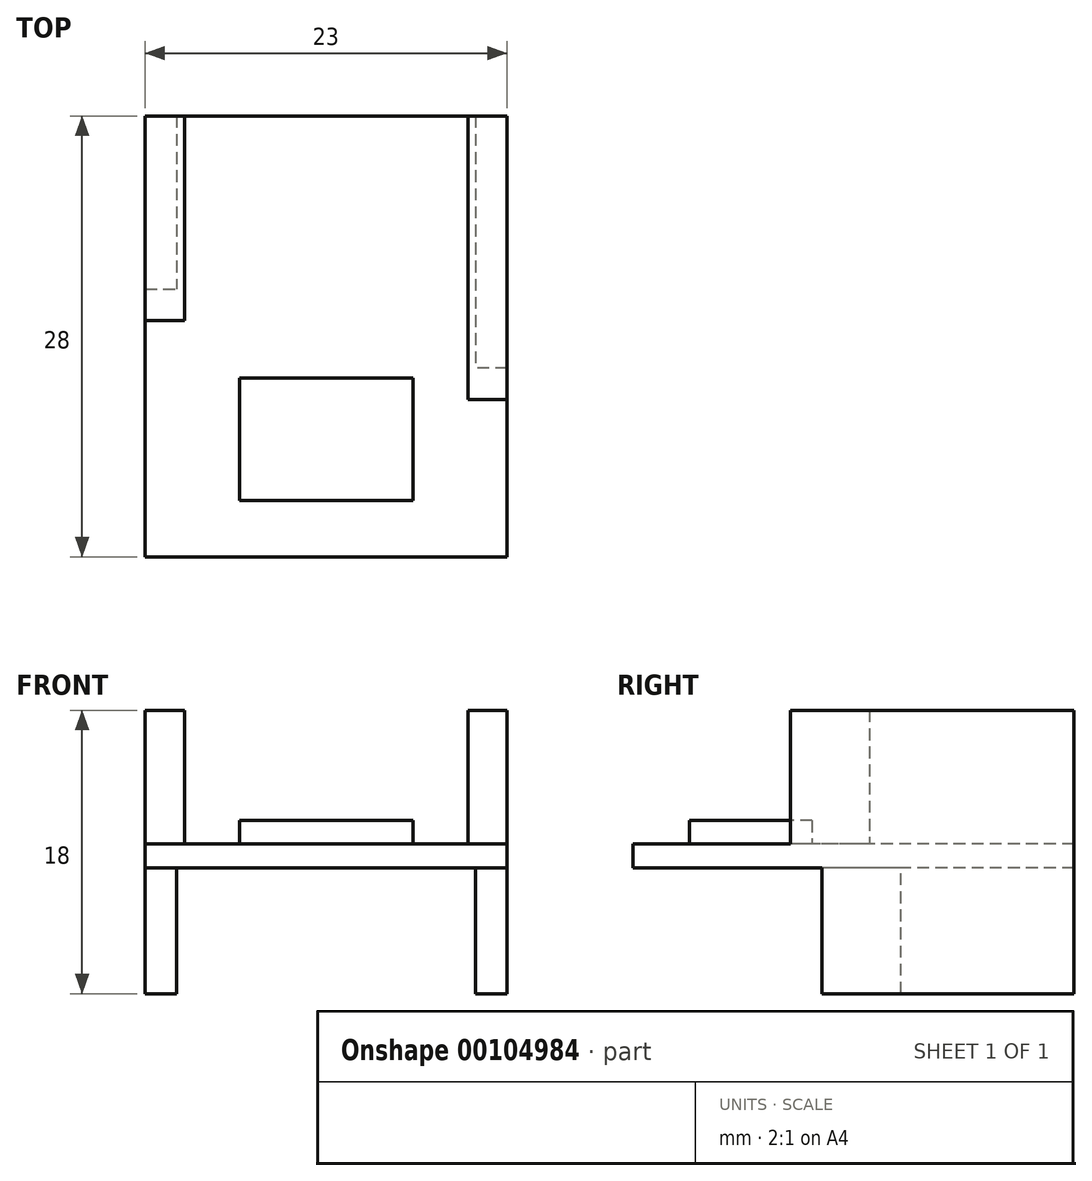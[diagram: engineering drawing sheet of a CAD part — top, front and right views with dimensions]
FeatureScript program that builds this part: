
annotation { "Feature Type Name" : "Feature", "Feature Type Description" : "" }
export const myFeature = defineFeature(function(context is Context, id is Id, definition is map)
    precondition{}
    {
        {
            var Q0;
            Q0=qCreatedBy(makeId("Top.planeOp"),FACE);
            var sketch = newSketch(context, id + "F0", { "sketchPlane" : qUnion([Q0])});
            skLineSegment(sketch, "E0.bottom", {"start": v(-11.5, 14) * mm, "end": v(11.5, 14) * mm});
            skLineSegment(sketch, "E0.top", {"start": v(-11.5, -14) * mm, "end": v(11.5, -14) * mm});
            skLineSegment(sketch, "E0.left", {"start": v(-11.5, 14) * mm, "end": v(-11.5, -14) * mm});
            skLineSegment(sketch, "E0.right", {"start": v(11.5, 14) * mm, "end": v(11.5, -14) * mm});
            skLineSegment(sketch, "E1", {"start": v(0, 14) * mm, "end": v(0, -14) * mm, "construction": true});
            skSolve(sketch);
        }
        {
            var Q0;
            Q0=makeQuery(id+"F0.imprint","IMPRINT",FACE,{"disambiguationData":[TD([[makeQuery(id+"F0.imprint","IMPRINT",EDGE,{"derivedFrom":sQuery(id+"F0.wireOp",EDGE,"E0.bottom")}),-1.0]])]});
            extrude(context, id + "F1", {"entities" : qUnion([Q0]), "depth" : 1.5 * mm});
        }
        {
            var Q0;
            Q0=makeQuery(id+"F1.opExtrude","CAP_FACE",FACE,{"disambiguationData":[OSD([sQuery(id+"F0.wireOp",EDGE,"E0.bottom"),sQuery(id+"F0.wireOp",EDGE,"E0.top"),sQuery(id+"F0.wireOp",EDGE,"E0.left"),sQuery(id+"F0.wireOp",EDGE,"E0.right")])],"isStart":false});
            var sketch = newSketch(context, id + "F2", { "sketchPlane" : qUnion([Q0])});
            skLineSegment(sketch, "E2.bottom", {"start": v(-11.5, 14) * mm, "end": v(-9, 14) * mm});
            skLineSegment(sketch, "E2.top", {"start": v(-11.5, 1) * mm, "end": v(-9, 1) * mm});
            skLineSegment(sketch, "E2.left", {"start": v(-11.5, 14) * mm, "end": v(-11.5, 1) * mm});
            skLineSegment(sketch, "E2.right", {"start": v(-9, 14) * mm, "end": v(-9, 1) * mm});
            skLineSegment(sketch, "E3.bottom", {"start": v(11.5, 14) * mm, "end": v(9, 14) * mm});
            skLineSegment(sketch, "E3.top", {"start": v(11.5, -4) * mm, "end": v(9, -4) * mm});
            skLineSegment(sketch, "E3.left", {"start": v(11.5, 14) * mm, "end": v(11.5, -4) * mm});
            skLineSegment(sketch, "E3.right", {"start": v(9, 14) * mm, "end": v(9, -4) * mm});
            skSolve(sketch);
        }
        {
            var Q0;
            Q0=makeQuery(id+"F2.imprint","IMPRINT",FACE,{"disambiguationData":[TD([[makeQuery(id+"F2.imprint","IMPRINT",EDGE,{"derivedFrom":sQuery(id+"F2.wireOp",EDGE,"E2.bottom")}),-1.0]])]});
            var Q1;
            Q1=makeQuery(id+"F2.imprint","IMPRINT",FACE,{"disambiguationData":[TD([[makeQuery(id+"F2.imprint","IMPRINT",EDGE,{"derivedFrom":sQuery(id+"F2.wireOp",EDGE,"E3.bottom")}),-1.0]])]});
            extrude(context, id + "F3", {"entities" : qUnion([Q0, Q1]), "operationType" : NewBodyOperationType.ADD, "depth" : 8.5 * mm});
        }
        {
            var Q0;
            Q0=makeQuery(id+"F1.opExtrude","CAP_FACE",FACE,{"disambiguationData":[OSD([sQuery(id+"F0.wireOp",EDGE,"E0.bottom"),sQuery(id+"F0.wireOp",EDGE,"E0.top"),sQuery(id+"F0.wireOp",EDGE,"E0.left"),sQuery(id+"F0.wireOp",EDGE,"E0.right")])],"isStart":true});
            var sketch = newSketch(context, id + "F4", { "sketchPlane" : qUnion([Q0])});
            skLineSegment(sketch, "E4.bottom", {"start": v(11.5, -14) * mm, "end": v(9.5, -14) * mm});
            skLineSegment(sketch, "E4.top", {"start": v(11.5, 2) * mm, "end": v(9.5, 2) * mm});
            skLineSegment(sketch, "E4.left", {"start": v(11.5, -14) * mm, "end": v(11.5, 2) * mm});
            skLineSegment(sketch, "E4.right", {"start": v(9.5, -14) * mm, "end": v(9.5, 2) * mm});
            skLineSegment(sketch, "E5.bottom", {"start": v(-11.5, -14) * mm, "end": v(-9.5, -14) * mm});
            skLineSegment(sketch, "E5.top", {"start": v(-11.5, -3) * mm, "end": v(-9.5, -3) * mm});
            skLineSegment(sketch, "E5.left", {"start": v(-11.5, -14) * mm, "end": v(-11.5, -3) * mm});
            skLineSegment(sketch, "E5.right", {"start": v(-9.5, -14) * mm, "end": v(-9.5, -3) * mm});
            skSolve(sketch);
        }
        {
            var Q0;
            Q0=makeQuery(id+"F4.imprint","IMPRINT",FACE,{"disambiguationData":[TD([[makeQuery(id+"F4.imprint","IMPRINT",EDGE,{"derivedFrom":sQuery(id+"F4.wireOp",EDGE,"E4.bottom")}),1.0]])]});
            var Q1;
            Q1=makeQuery(id+"F4.imprint","IMPRINT",FACE,{"disambiguationData":[TD([[makeQuery(id+"F4.imprint","IMPRINT",EDGE,{"derivedFrom":sQuery(id+"F4.wireOp",EDGE,"E5.bottom")}),1.0]])]});
            extrude(context, id + "F5", {"entities" : qUnion([Q0, Q1]), "operationType" : NewBodyOperationType.ADD, "depth" : 8 * mm});
        }
        {
            var Q0;
            Q0=makeQuery(id+"F1.opExtrude","CAP_FACE",FACE,{"disambiguationData":[OSD([sQuery(id+"F0.wireOp",EDGE,"E0.bottom"),sQuery(id+"F0.wireOp",EDGE,"E0.top"),sQuery(id+"F0.wireOp",EDGE,"E0.left"),sQuery(id+"F0.wireOp",EDGE,"E0.right")])],"isStart":false});
            var sketch = newSketch(context, id + "F6", { "sketchPlane" : qUnion([Q0])});
            skLineSegment(sketch, "E6.bottom", {"start": v(5.51, -2.63) * mm, "end": v(-5.51, -2.63) * mm});
            skLineSegment(sketch, "E6.top", {"start": v(5.51, -10.42) * mm, "end": v(-5.51, -10.42) * mm});
            skLineSegment(sketch, "E6.left", {"start": v(5.51, -2.63) * mm, "end": v(5.51, -10.42) * mm});
            skLineSegment(sketch, "E6.right", {"start": v(-5.51, -2.63) * mm, "end": v(-5.51, -10.42) * mm});
            skPoint(sketch, "E6.middle", {"position": v(0, -6.53) * mm});
            skSolve(sketch);
        }
        {
            var Q0;
            Q0=makeQuery(id+"F6.imprint","IMPRINT",FACE,{"disambiguationData":[TD([[makeQuery(id+"F6.imprint","IMPRINT",EDGE,{"derivedFrom":sQuery(id+"F6.wireOp",EDGE,"E6.bottom")}),1.0]])]});
            extrude(context, id + "F7", {"entities" : qUnion([Q0]), "operationType" : NewBodyOperationType.ADD, "depth" : 1.5 * mm});
        }
    });
